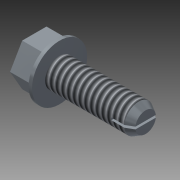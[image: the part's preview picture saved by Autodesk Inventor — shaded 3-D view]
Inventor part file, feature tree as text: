
AUTODESK INVENTOR PART (.ipt)
format: ipt  version: 2016 SP1 (Build 200210100, 210)  size: 122,880 bytes
history: native  units: in
note: dims shown in document units (in); Inventor stores cm internally (conversion verified against a paired STEP export)
features: thread x1, other x1
ambient origin geometry x8: Origin, YZ Plane, XZ Plane, XY Plane, X Axis, Y Axis, Z Axis, Center Point
bodies: Solid1 (feature_tree)
feature tree (2):
  thread  "Thread1"  [1 undecoded]
  other  "point_Cut-Extrude10"
note: 1 required parameter value undecoded (feature->parameter linkage not recoverable at this tier; creation-order binding heuristic only, values carry confidence <= 0.55)
